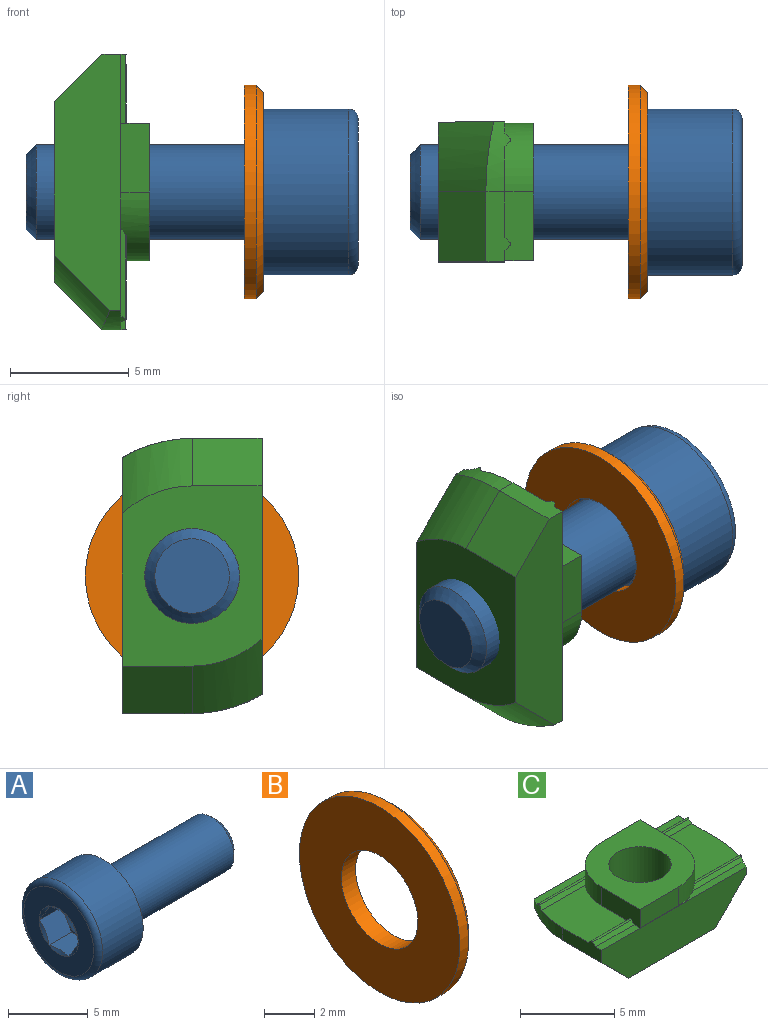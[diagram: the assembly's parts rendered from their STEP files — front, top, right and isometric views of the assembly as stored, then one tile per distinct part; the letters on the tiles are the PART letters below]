
ASSEMBLY  parts=3 mates=2
PART A: 24 faces, bbox 14x7.6x7.6 mm
  f0: plane 1.3x0.75mm, normal (-1,0,0), area 0.1mm2, adj f16,f17,f23
  f1: plane 1.5x0.43mm, normal (-1,0,0), area 0.1mm2, adj f17,f18,f23
  f2: plane 1.3x0.75mm, normal (-1,0,0), area 0.1mm2, adj f18,f19,f23
  f3: plane 1.3x0.75mm, normal (-1,0,0), area 0.1mm2, adj f19,f20,f23
  f4: plane 1.5x0.43mm, normal (-1,0,0), area 0.1mm2, adj f20,f21,f23
  f5: cone r=1.74mm half-angle=60deg, axis (-1,0,0), area 2mm2, adj f15,f16,f17,f18,f19,f20,f21
  f6: cone r=2.01mm half-angle=20.6deg, axis (-1,0,0), area 5.6mm2, adj f7,f11
  f7: torus R=2.2mm, axis (1,0,0), area 0.9mm2, adj f6,f10
  f8: plane 3.14x3.14mm, normal (1,0,0), area 7.7mm2, adj f9
  f9: cone r=2mm half-angle=45deg, axis (-1,0,0), area 6.8mm2, adj f8,f10
  f10: cylinder r=2mm len=8.97mm, axis (1,0,0), area 112.7mm2, adj f7,f9
  f11: torus R=2.35mm, axis (1,0,0), area 3.4mm2, adj f6,f13
  f12: cylinder r=3.5mm len=7mm, axis (1,0,0), area 79.2mm2, adj f13,f14
  f13: plane 7x7mm, normal (1,0,0), area 21.1mm2, adj f11,f12
  f14: torus R=3.1mm, axis (1,0,0), area 13.2mm2, adj f12,f15
  f15: plane 6.2x6.2mm, normal (-1,0,0), area 20.7mm2, adj f5,f14
  f16: plane 2x1.74mm, normal (0,0,-1), area 3.3mm2, adj f0,f5,f17,f21,f22
  f17: plane 2x1.5mm, normal (0,0.87,-0.5), area 3.3mm2, adj f0,f1,f5,f16,f18
  f18: plane 2x1.5mm, normal (0,0.87,0.5), area 3.3mm2, adj f1,f2,f5,f17,f19
  f19: plane 2x1.74mm, normal (0,0,1), area 3.3mm2, adj f2,f3,f5,f18,f20
  f20: plane 2x1.5mm, normal (0,-0.87,0.5), area 3.3mm2, adj f3,f4,f5,f19,f21
  f21: plane 2x1.5mm, normal (0,-0.87,-0.5), area 3.3mm2, adj f4,f5,f16,f20,f22
  f22: plane 1.3x0.75mm, normal (-1,0,0), area 0.1mm2, adj f16,f21,f23
  f23: cone r=1.5mm half-angle=60deg, axis (-1,0,0), area 8.2mm2, adj f0,f1,f2,f3,f4,f22
PART B: 5 faces, bbox 0.8x9x9 mm
  f0: plane 9x9mm, normal (-1,0,0), area 49.1mm2, adj f1,f4
  f1: cylinder r=2.15mm len=4.3mm, axis (1,0,0), area 10.8mm2, adj f0,f2
  f2: plane 8.4x8.4mm, normal (1,0,0), area 40.9mm2, adj f1,f3
  f3: cone r=4.2mm half-angle=45deg, axis (-1,0,0), area 11.6mm2, adj f2,f4
  f4: cylinder r=4.5mm len=9mm, axis (1,0,0), area 14.1mm2, adj f0,f3
PART C: 35 faces, bbox 11.6x5.9x4.6 mm
  f0: cylinder r=1.65mm len=4mm, axis (0,0,1), area 41.5mm2, adj f7,f26
  f1: cylinder r=2.9mm len=2.9mm, axis (0,0,1), area 5.4mm2, adj f2,f5,f7,f8,f10,f12,f14,f33
  f2: plane 2.9x1.2mm, normal (1,0,0), area 3.4mm2, adj f1,f6,f7,f14,f16,f18,f20,f22
  f3: cylinder r=2.9mm len=2.9mm, axis (0,0,1), area 5.4mm2, adj f4,f6,f7,f15,f17,f19,f21,f22
  f4: plane 2.9x1.2mm, normal (-1,0,0), area 3.4mm2, adj f3,f5,f7,f9,f11,f13,f15,f33
  f5: plane 2.9x1.2mm, normal (0,-1,0), area 3.5mm2, adj f1,f4,f7,f33
  f6: plane 2.9x1.2mm, normal (0,1,0), area 3.5mm2, adj f2,f3,f7,f22
  f7: plane 5.8x5.8mm, normal (0,0,1), area 21.5mm2, adj f0,f1,f2,f3,f4,f5,f6
  f8: plane 3.83x0.21mm, normal (0,-0.71,0.71), area 1mm2, adj f1,f10,f32,f33
  f9: plane 2.9x0.2mm, normal (0,-0.71,0.71), area 0.8mm2, adj f4,f11,f30,f33
  f10: cylinder r=0.1mm len=3.59mm, axis (1,0,0), area 0.5mm2, adj f1,f8,f12,f32
  f11: cylinder r=0.1mm len=2.9mm, axis (1,0,0), area 0.5mm2, adj f4,f9,f13,f30
  f12: plane 3.51x0.21mm, normal (0,0.71,0.71), area 1mm2, adj f1,f10,f14,f32
  f13: plane 2.9x0.2mm, normal (0,0.71,0.71), area 0.8mm2, adj f4,f11,f15,f30
  f14: plane 3.85x3.63mm, normal (0,0,1), area 11.4mm2, adj f1,f2,f12,f16,f32,f34
  f15: plane 3.85x3.63mm, normal (0,0,1), area 11.4mm2, adj f3,f4,f13,f17,f29,f30
  f16: plane 2.9x0.2mm, normal (0,-0.71,0.71), area 0.8mm2, adj f2,f14,f18,f34
  f17: plane 3.51x0.21mm, normal (0,-0.71,0.71), area 1mm2, adj f3,f15,f19,f29
  f18: cylinder r=0.1mm len=2.9mm, axis (1,0,0), area 0.5mm2, adj f2,f16,f20,f34
  f19: cylinder r=0.1mm len=3.59mm, axis (1,0,0), area 0.5mm2, adj f3,f17,f21,f29
  f20: plane 2.9x0.2mm, normal (0,0.71,0.71), area 0.8mm2, adj f2,f18,f22,f34
  f21: plane 3.83x0.21mm, normal (0,0.71,0.71), area 1mm2, adj f3,f19,f22,f29
  f22: plane 11.05x0.48mm, normal (0,0,1), area 3.5mm2, adj f2,f3,f6,f20,f21,f25,f29,f34
  f23: plane 2.95x2mm, normal (0.71,0,-0.71), area 8.3mm2, adj f24,f25,f26,f34
  f24: cylinder r=5.8mm len=3.14mm, axis (0.71,0,0.71), area 9.2mm2, adj f23,f26,f31,f32
  f25: plane 10.79x2.8mm, normal (0,1,0), area 25.5mm2, adj f22,f23,f26,f28,f29,f34
  f26: plane 7.6x5.9mm, normal (0,0,-1), area 34.1mm2, adj f0,f23,f24,f25,f27,f28,f31
  f27: plane 2.95x2mm, normal (-0.71,0,-0.71), area 8.3mm2, adj f26,f28,f30,f31
  f28: cylinder r=5.8mm len=3.14mm, axis (-0.71,0,0.71), area 9.2mm2, adj f25,f26,f27,f29
  f29: cylinder r=5.8mm len=2.95mm, axis (0,0,1), area 2.2mm2, adj f15,f17,f19,f21,f22,f25,f28,f30
  f30: plane 2.95x1.03mm, normal (-1,0,0), area 2.4mm2, adj f9,f11,f13,f15,f27,f29,f31,f33
  f31: plane 10.79x2.8mm, normal (0,-1,0), area 25.5mm2, adj f24,f26,f27,f30,f32,f33
  f32: cylinder r=5.8mm len=2.95mm, axis (0,0,1), area 2.2mm2, adj f8,f10,f12,f14,f24,f31,f33,f34
  f33: plane 11.05x0.48mm, normal (0,0,1), area 3.5mm2, adj f1,f4,f5,f8,f9,f30,f31,f32
  f34: plane 2.95x1.03mm, normal (1,0,0), area 2.4mm2, adj f14,f16,f18,f20,f22,f23,f25,f32
PLACE A rot(axis=(0,1,0),180deg) t=(-1.79,0.22,2.23)mm
PLACE B t=(-2.59,0.22,2.23)mm fixed
PLACE C rot(axis=(-0.71,0,-0.71),180deg) t=(-7.56,0.22,2.23)mm
MATE fastened C.f0 <-> B.f1  axis (1,0,0) through (-6.59,0.22,2.23)mm
MATE fastened A.f5 <-> B.f1  axis (-1,0,0) through (-1.79,0.22,2.23)mm
